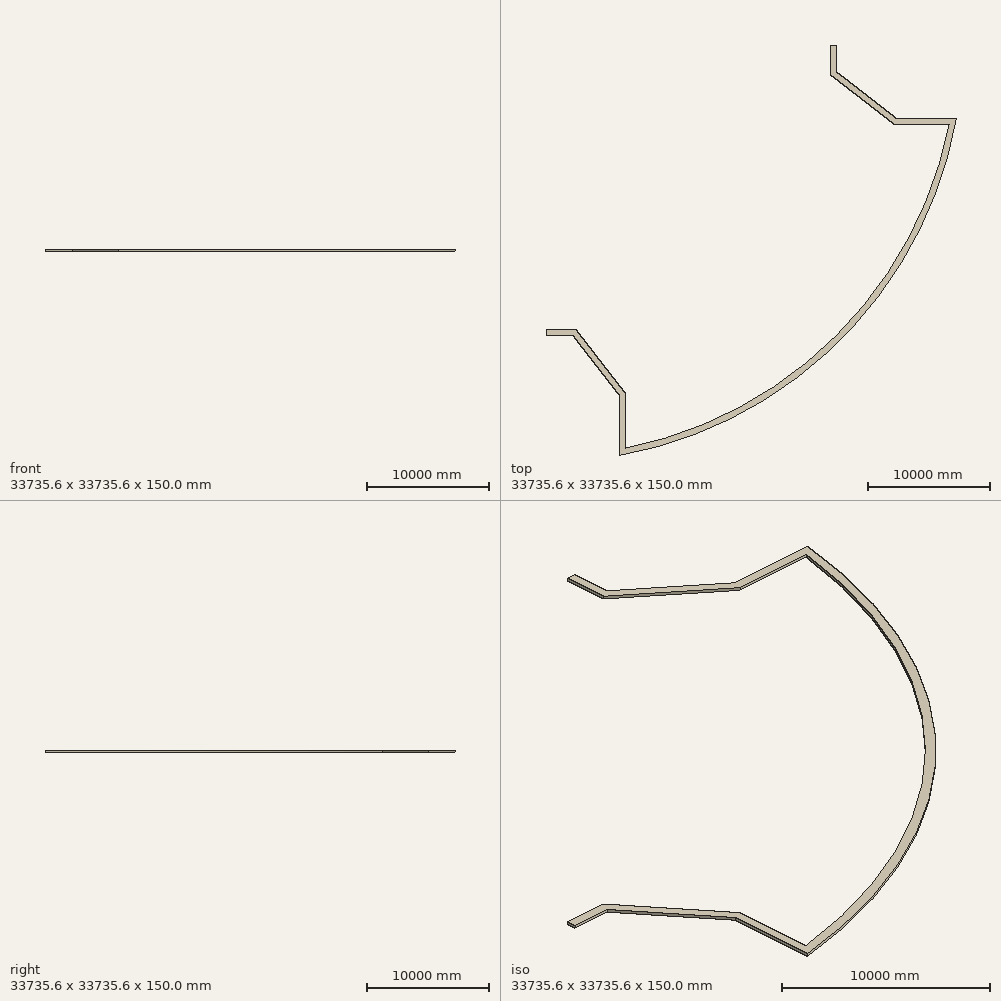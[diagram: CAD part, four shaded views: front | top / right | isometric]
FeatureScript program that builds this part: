
annotation { "Feature Type Name" : "Feature", "Feature Type Description" : "" }
export const myFeature = defineFeature(function(context is Context, id is Id, definition is map)
    precondition{}
    {
        {
            var Q0;
            Q0=qCreatedBy(makeId("Top.planeOp"),FACE);
            var sketch = newSketch(context, id + "F0", { "sketchPlane" : qUnion([Q0])});
            skArc(sketch, "E0", {"start": v(0, -34265) * mm, "mid": v(24229.01, -24229.01) * mm, "end": v(34265, 0) * mm, "construction": true});
            skArc(sketch, "E1", {"start": v(0, -33765) * mm, "mid": v(23875.46, -23875.46) * mm, "end": v(33765, 0) * mm, "construction": true});
            skArc(sketch, "E2", {"start": v(0, -34015) * mm, "mid": v(24052.24, -24052.24) * mm, "end": v(34015, 0) * mm, "construction": true});
            skLineSegment(sketch, "E3", {"start": v(0, 0) * mm, "end": v(34265, 0) * mm, "construction": true});
            skLineSegment(sketch, "E4", {"start": v(34265, 0) * mm, "end": v(0, 0) * mm, "construction": true});
            skLineSegment(sketch, "E5", {"start": v(0, -34265) * mm, "end": v(0, 0) * mm, "construction": true});
            skSolve(sketch);
        }
        {
            var Q0;
            Q0=qCreatedBy(makeId("Top.planeOp"),FACE);
            var sketch = newSketch(context, id + "F1", { "sketchPlane" : qUnion([Q0])});
            skLineSegment(sketch, "E6", {"start": v(0, -23402.61) * mm, "end": v(0, -23902.61) * mm});
            skArc(sketch, "E7", {"start": v(6000, -33735.6) * mm, "mid": v(24229.01, -24229.01) * mm, "end": v(33735.6, -6000) * mm});
            skLineSegment(sketch, "E8", {"start": v(23402.61, 0) * mm, "end": v(23902.61, 0) * mm});
            skLineSegment(sketch, "E9", {"start": v(28801.6, -6000) * mm, "end": v(33735.6, -6000) * mm});
            skLineSegment(sketch, "E10", {"start": v(23902.61, 0) * mm, "end": v(23902.61, -2200) * mm});
            skLineSegment(sketch, "E11", {"start": v(23902.61, -2200) * mm, "end": v(28801.6, -6000) * mm});
            skLineSegment(sketch, "E12", {"start": v(6000, -33735.6) * mm, "end": v(6000, -28801.6) * mm});
            skLineSegment(sketch, "E13", {"start": v(0, -23902.61) * mm, "end": v(2200, -23902.61) * mm});
            skLineSegment(sketch, "E14", {"start": v(2200, -23902.61) * mm, "end": v(6000, -28801.6) * mm});
            skLineSegment(sketch, "E15", {"start": v(23402.61, 0) * mm, "end": v(23402.61, -2444.95) * mm});
            skLineSegment(sketch, "E16", {"start": v(23402.61, -2444.95) * mm, "end": v(28630.4, -6500) * mm});
            skLineSegment(sketch, "E17", {"start": v(28630.4, -6500) * mm, "end": v(33133.45, -6500) * mm});
            skArc(sketch, "E18", {"start": v(6500, -33133.45) * mm, "mid": v(23875.46, -23875.46) * mm, "end": v(33133.45, -6500) * mm});
            skLineSegment(sketch, "E19", {"start": v(6500, -28630.4) * mm, "end": v(6500, -33133.45) * mm});
            skLineSegment(sketch, "E20", {"start": v(6500, -28630.4) * mm, "end": v(2444.95, -23402.61) * mm});
            skLineSegment(sketch, "E21", {"start": v(2444.95, -23402.61) * mm, "end": v(0, -23402.61) * mm});
            skSolve(sketch);
        }
        {
            var Q0;
            Q0=makeQuery(id+"F1.imprint","IMPRINT",FACE,{"disambiguationData":[TD([[makeQuery(id+"F1.imprint","IMPRINT",EDGE,{"derivedFrom":sQuery(id+"F1.wireOp",EDGE,"E6")}),1.0]])]});
            extrude(context, id + "F2", {"entities" : qUnion([Q0]), "depth" : 150 * mm});
        }
    });
